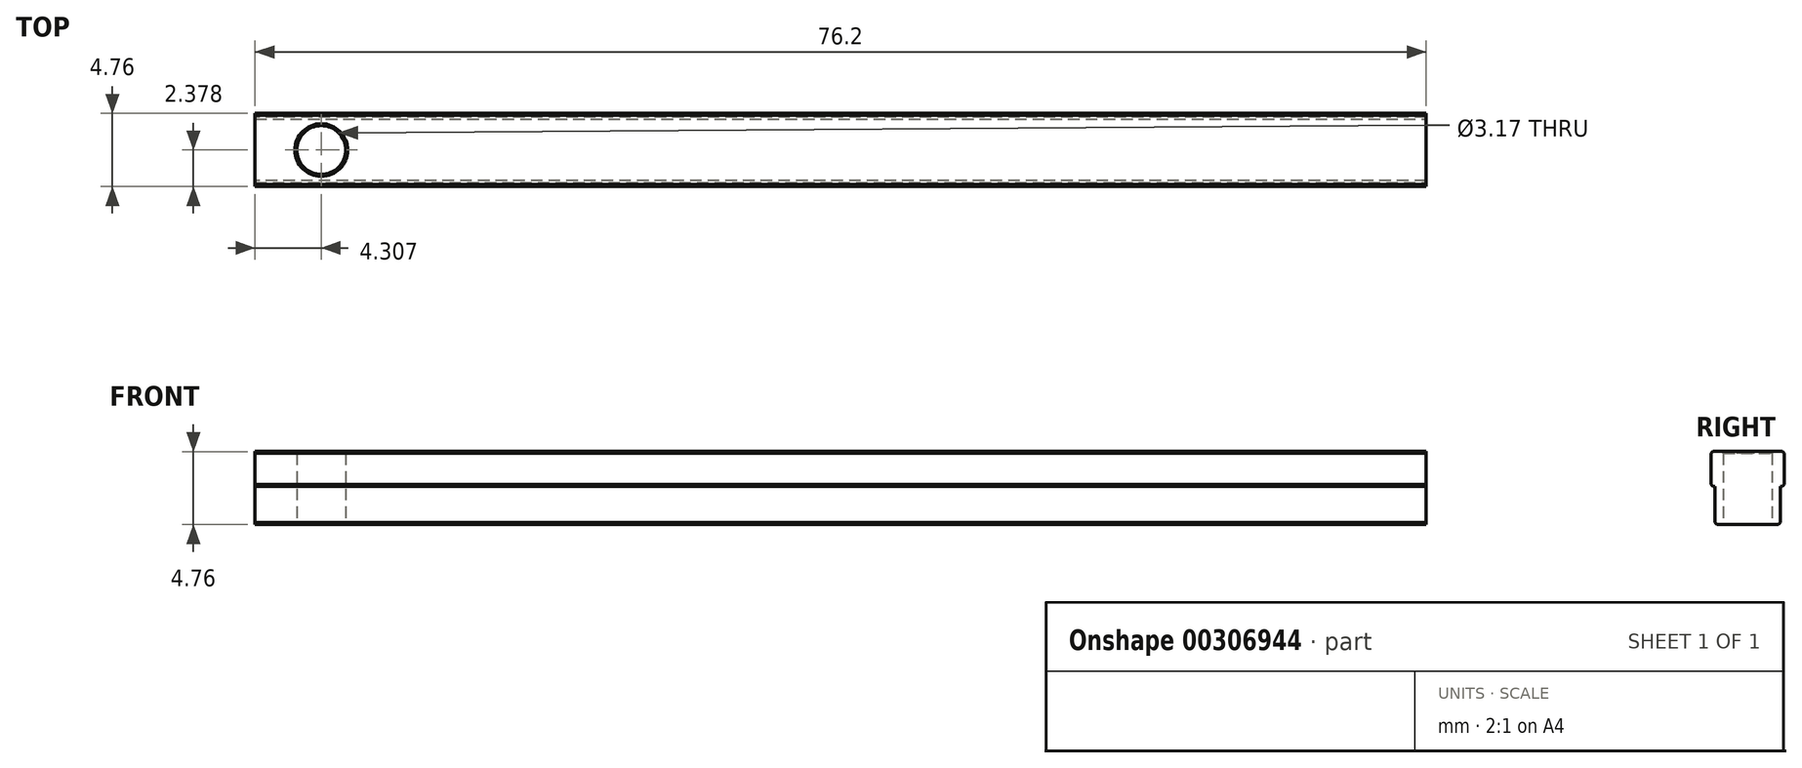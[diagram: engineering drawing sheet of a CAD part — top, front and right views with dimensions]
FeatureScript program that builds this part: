
annotation { "Feature Type Name" : "Feature", "Feature Type Description" : "" }
export const myFeature = defineFeature(function(context is Context, id is Id, definition is map)
    precondition{}
    {
        {
            var Q0;
            Q0=qCreatedBy(makeId("Right.planeOp"),FACE);
            var sketch = newSketch(context, id + "F0", { "sketchPlane" : qUnion([Q0])});
            skLineSegment(sketch, "E0.bottom", {"start": v(2.38, -2.29) * mm, "end": v(-2.38, -2.29) * mm});
            skLineSegment(sketch, "E0.top", {"start": v(2.13, 2.48) * mm, "end": v(-2.13, 2.48) * mm});
            skLineSegment(sketch, "E0.left", {"start": v(2.38, -2.29) * mm, "end": v(2.38, 0) * mm});
            skLineSegment(sketch, "E0.right", {"start": v(-2.38, -2.29) * mm, "end": v(-2.38, 0) * mm});
            skPoint(sketch, "E0.middle", {"position": v(0, 0) * mm});
            skLineSegment(sketch, "E1", {"start": v(-2.38, 0) * mm, "end": v(-2.13, 0) * mm});
            skLineSegment(sketch, "E2", {"start": v(-2.13, 2.48) * mm, "end": v(-2.13, 0) * mm});
            skLineSegment(sketch, "E3", {"start": v(2.13, 0) * mm, "end": v(2.13, 2.48) * mm});
            skLineSegment(sketch, "E4.trimOffspring", {"start": v(2.13, 0) * mm, "end": v(2.38, 0) * mm});
            skSolve(sketch);
        }
        {
            var Q0;
            Q0=makeQuery(id+"F0.imprint","IMPRINT",FACE,{"disambiguationData":[TD([[makeQuery(id+"F0.imprint","IMPRINT",EDGE,{"derivedFrom":sQuery(id+"F0.wireOp",EDGE,"E0.bottom")}),-1.0]])]});
            extrude(context, id + "F1", {"entities" : qUnion([Q0]), "oppositeDirection" : true, "depth" : 76.2 * mm});
        }
        {
            var Q0;
            Q0=makeQuery(id+"F1.opExtrude","SWEPT_FACE",FACE,{"disambiguationData":[OSD([sQuery(id+"F0.wireOp",EDGE,"E0.top")])]});
            var sketch = newSketch(context, id + "F2", { "sketchPlane" : qUnion([Q0])});
            skCircle(sketch, "E5", {"center": v(-71.9, 0) * mm, "radius": 1.59 * mm});
            skPoint(sketch, "E5.centerSnap0", {"position": v(-76.2, 0) * mm});
            skSolve(sketch);
        }
        {
            var Q0;
            Q0=makeQuery(id+"F2.imprint","IMPRINT",FACE,{"disambiguationData":[TD([[makeQuery(id+"F2.imprint","IMPRINT",EDGE,{"derivedFrom":sQuery(id+"F2.wireOp",EDGE,"E5")}),1.0]])]});
            extrude(context, id + "F3", {"entities" : qUnion([Q0]), "operationType" : NewBodyOperationType.REMOVE, "endBound" : BoundingType.THROUGH_ALL, "oppositeDirection" : true, "depth" : 25.4 * mm});
        }
        {
            var Q0;
            Q0=makeQuery(id+"F1.opExtrude","SWEPT_EDGE",EDGE,{"disambiguationData":[OSD([sQuery(id+"F0.wireOp",EDGE,"E0.top"),sQuery(id+"F0.wireOp",EDGE,"E0.right")])]});
            var Q1;
            Q1=makeQuery(id+"F1.opExtrude","SWEPT_EDGE",EDGE,{"disambiguationData":[OSD([sQuery(id+"F0.wireOp",EDGE,"E0.bottom"),sQuery(id+"F0.wireOp",EDGE,"E0.right")])]});
            var Q2;
            Q2=makeQuery(id+"F1.opExtrude","SWEPT_EDGE",EDGE,{"disambiguationData":[OSD([sQuery(id+"F0.wireOp",EDGE,"E0.top"),sQuery(id+"F0.wireOp",EDGE,"E0.left")])]});
            var Q3;
            Q3=makeQuery(id+"F1.opExtrude","SWEPT_EDGE",EDGE,{"disambiguationData":[OSD([sQuery(id+"F0.wireOp",EDGE,"E0.bottom"),sQuery(id+"F0.wireOp",EDGE,"E0.left")])]});
            var Q4;
            Q4=makeQuery(id+"F3.boolean.opBoolean","COPY",EDGE,{"derivedFrom":makeQuery(id+"F3.opExtrude","CAP_EDGE",EDGE,{"disambiguationData":[OSD([sQuery(id+"F2.wireOp",EDGE,"E5")])],"isStart":true})});
            var Q5;
            Q5=makeQuery(id+"F3.boolean.opBoolean","INTERSECT",EDGE,{"derivedFrom":[makeQuery(id+"F1.opExtrude","SWEPT_FACE",FACE,{"disambiguationData":[OSD([sQuery(id+"F0.wireOp",EDGE,"E0.bottom")])]}),makeQuery(id+"F3.opExtrude","SWEPT_FACE",FACE,{"disambiguationData":[OSD([sQuery(id+"F2.wireOp",EDGE,"E5")])]})]});
            chamfer(context, id + "F4", {"entities" : qUnion([Q0, Q1, Q2, Q3, Q4, Q5]), "width" : 0.13 * mm, "tangentPropagation" : true});
        }
        {
            var Q0;
            Q0=makeQuery(id+"F1.opExtrude","SWEPT_BODY",BODY,{"disambiguationData":[OSD([sQuery(id+"F0.wireOp",EDGE,"E0.bottom"),sQuery(id+"F0.wireOp",EDGE,"E0.top"),sQuery(id+"F0.wireOp",EDGE,"E0.left"),sQuery(id+"F0.wireOp",EDGE,"E0.right"),sQuery(id+"F0.wireOp",EDGE,"E1"),sQuery(id+"F0.wireOp",EDGE,"E2"),sQuery(id+"F0.wireOp",EDGE,"E3"),sQuery(id+"F0.wireOp",EDGE,"E4.trimOffspring")])]});
            var Q1;
            {var subQ0=sQuery(id+"F0.wireOp",EDGE,"E0.bottom");Q1=makeQuery(id+"F4.opChamfer","BLEND_EDGE",EDGE,{"blendedFrom":[makeQuery(id+"F1.opExtrude","SWEPT_EDGE",EDGE,{"disambiguationData":[OSD([subQ0,sQuery(id+"F0.wireOp",EDGE,"E0.left")])]}),makeQuery(id+"F1.opExtrude","SWEPT_FACE",FACE,{"disambiguationData":[OSD([subQ0])]})],"blendedInto":[makeQuery(id+"F1.opExtrude","SWEPT_FACE",FACE,{"disambiguationData":[OSD([subQ0])]})]});}
            transform(context, id + "F5", {"entities" : qUnion([Q0]), "transformType" : TransformType.ROTATION, "transformAxis" : qUnion([Q1]), "angle" : 180 * degree, "makeCopy" : false});
        }
    });
